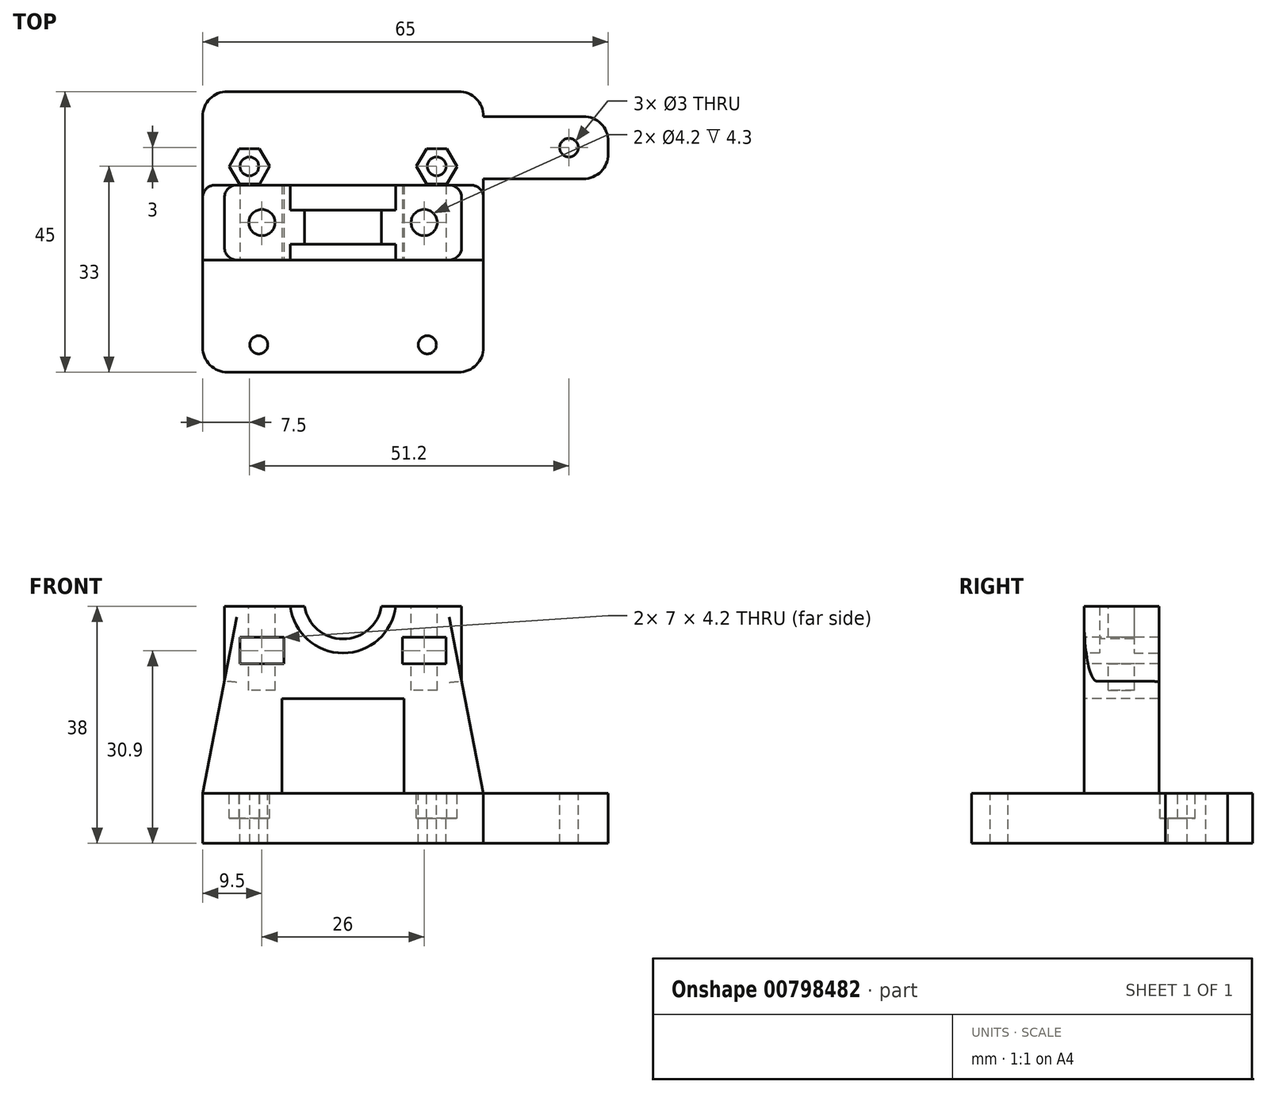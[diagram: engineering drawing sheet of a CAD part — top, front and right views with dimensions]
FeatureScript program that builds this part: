
annotation { "Feature Type Name" : "Feature", "Feature Type Description" : "" }
export const myFeature = defineFeature(function(context is Context, id is Id, definition is map)
    precondition{}
    {
        {
            var Q0;
            Q0=qCreatedBy(makeId("Top.planeOp"),FACE);
            var sketch = newSketch(context, id + "F0", { "sketchPlane" : qUnion([Q0])});
            skLineSegment(sketch, "E0.bottom", {"start": v(22.5, 22.5) * mm, "end": v(-22.5, 22.5) * mm});
            skLineSegment(sketch, "E0.top", {"start": v(22.5, -22.5) * mm, "end": v(-22.5, -22.5) * mm});
            skLineSegment(sketch, "E0.left", {"start": v(22.5, 22.5) * mm, "end": v(22.5, -22.5) * mm});
            skLineSegment(sketch, "E0.right", {"start": v(-22.5, 22.5) * mm, "end": v(-22.5, -22.5) * mm});
            skPoint(sketch, "E0.middle", {"position": v(0, 0) * mm});
            skLineSegment(sketch, "E1.bottom", {"start": v(22.5, 8.5) * mm, "end": v(42.5, 8.5) * mm});
            skLineSegment(sketch, "E1.top", {"start": v(22.5, 18.5) * mm, "end": v(42.5, 18.5) * mm});
            skLineSegment(sketch, "E1.left", {"start": v(22.5, 8.5) * mm, "end": v(22.5, 18.5) * mm});
            skLineSegment(sketch, "E1.right", {"start": v(42.5, 8.5) * mm, "end": v(42.5, 18.5) * mm});
            skSolve(sketch);
        }
        {
            var Q0;
            {var subQ3=sQuery(id+"F0.wireOp",EDGE,"E0.bottom");Q0=makeQuery(id+"F0.imprint","IMPRINT",FACE,{"disambiguationData":[TD([[makeQuery(id+"F0.imprint","IMPRINT",EDGE,{"derivedFrom":subQ3}),1.0]])]});}
            var Q1;
            Q1=makeQuery(id+"F0.imprint","IMPRINT",FACE,{"disambiguationData":[TD([[makeQuery(id+"F0.imprint","IMPRINT",EDGE,{"derivedFrom":sQuery(id+"F0.wireOp",EDGE,"E1.bottom")}),1.0]])]});
            extrude(context, id + "F1", {"entities" : qUnion([Q0, Q1]), "depth" : 8 * mm, "offsetDistance" : 25 * mm});
        }
        {
            var Q0;
            Q0=makeQuery(id+"F1.opExtrude","CAP_FACE",FACE,{"disambiguationData":[OSD([sQuery(id+"F0.wireOp",EDGE,"E0.bottom"),sQuery(id+"F0.wireOp",EDGE,"E0.top"),sQuery(id+"F0.wireOp",EDGE,"E0.left"),sQuery(id+"F0.wireOp",EDGE,"E0.right"),sQuery(id+"F0.wireOp",EDGE,"E1.bottom"),sQuery(id+"F0.wireOp",EDGE,"E1.top"),sQuery(id+"F0.wireOp",EDGE,"E1.right")])],"isStart":false});
            var sketch = newSketch(context, id + "F2", { "sketchPlane" : qUnion([Q0])});
            skLineSegment(sketch, "E2.bottom", {"start": v(-22.5, -4.5) * mm, "end": v(22.5, -4.5) * mm});
            skLineSegment(sketch, "E2.top", {"start": v(-22.5, 7.5) * mm, "end": v(22.5, 7.5) * mm});
            skLineSegment(sketch, "E2.left", {"start": v(-22.5, -4.5) * mm, "end": v(-22.5, 7.5) * mm});
            skLineSegment(sketch, "E2.right", {"start": v(22.5, -4.5) * mm, "end": v(22.5, 7.5) * mm});
            skSolve(sketch);
        }
        {
            var Q0;
            Q0=makeQuery(id+"F2.imprint","IMPRINT",FACE,{"disambiguationData":[TD([[makeQuery(id+"F2.imprint","IMPRINT",EDGE,{"derivedFrom":sQuery(id+"F2.wireOp",EDGE,"E2.bottom")}),1.0]])]});
            extrude(context, id + "F3", {"entities" : qUnion([Q0]), "operationType" : NewBodyOperationType.ADD, "depth" : 18 * mm, "offsetDistance" : 25 * mm});
        }
        {
            var Q0;
            Q0=makeQuery(id+"F3.opExtrude","CAP_FACE",FACE,{"disambiguationData":[OSD([sQuery(id+"F2.wireOp",EDGE,"E2.bottom"),sQuery(id+"F2.wireOp",EDGE,"E2.top"),sQuery(id+"F2.wireOp",EDGE,"E2.left"),sQuery(id+"F2.wireOp",EDGE,"E2.right")])],"isStart":false});
            var sketch = newSketch(context, id + "F4", { "sketchPlane" : qUnion([Q0])});
            skLineSegment(sketch, "E3.bottom", {"start": v(-19, 7.5) * mm, "end": v(19, 7.5) * mm});
            skLineSegment(sketch, "E3.top", {"start": v(-19, -4.5) * mm, "end": v(19, -4.5) * mm});
            skLineSegment(sketch, "E3.left", {"start": v(-19, 7.5) * mm, "end": v(-19, -4.5) * mm});
            skLineSegment(sketch, "E3.right", {"start": v(19, 7.5) * mm, "end": v(19, -4.5) * mm});
            skSolve(sketch);
        }
        {
            var Q0;
            Q0=makeQuery(id+"F4.imprint","IMPRINT",FACE,{"disambiguationData":[TD([[makeQuery(id+"F4.imprint","IMPRINT",EDGE,{"derivedFrom":sQuery(id+"F4.wireOp",EDGE,"E3.bottom")}),-1.0]])]});
            extrude(context, id + "F5", {"entities" : qUnion([Q0]), "operationType" : NewBodyOperationType.ADD, "depth" : 12 * mm, "offsetDistance" : 25 * mm});
        }
        {
            var Q0;
            Q0=makeQuery(id+"F5.boolean.opBoolean","MERGE",FACE,{"derivedFrom":[makeQuery(id+"F3.opExtrude","SWEPT_FACE",FACE,{"disambiguationData":[OSD([sQuery(id+"F2.wireOp",EDGE,"E2.bottom")])]}),makeQuery(id+"F5.opExtrude","SWEPT_FACE",FACE,{"disambiguationData":[OSD([sQuery(id+"F4.wireOp",EDGE,"E3.top")])]})]});
            var sketch = newSketch(context, id + "F6", { "sketchPlane" : qUnion([Q0])});
            skLineSegment(sketch, "E4", {"start": v(-19, 26) * mm, "end": v(-22.5, 8) * mm});
            skLineSegment(sketch, "E5", {"start": v(-22.5, 8) * mm, "end": v(-22.5, 26) * mm});
            skLineSegment(sketch, "E6", {"start": v(-22.5, 26) * mm, "end": v(-19, 26) * mm});
            skLineSegment(sketch, "E7", {"start": v(19, 26) * mm, "end": v(22.5, 26) * mm});
            skLineSegment(sketch, "E8", {"start": v(22.5, 26) * mm, "end": v(22.5, 8) * mm});
            skLineSegment(sketch, "E9", {"start": v(22.5, 8) * mm, "end": v(19, 26) * mm});
            skSolve(sketch);
        }
        {
            var Q0;
            Q0=makeQuery(id+"F6.imprint","IMPRINT",FACE,{"disambiguationData":[TD([[makeQuery(id+"F6.imprint","IMPRINT",EDGE,{"derivedFrom":sQuery(id+"F6.wireOp",EDGE,"E4")}),-1.0]])]});
            var Q1;
            Q1=makeQuery(id+"F6.imprint","IMPRINT",FACE,{"disambiguationData":[TD([[makeQuery(id+"F6.imprint","IMPRINT",EDGE,{"derivedFrom":sQuery(id+"F6.wireOp",EDGE,"E7")}),-1.0]])]});
            extrude(context, id + "F7", {"entities" : qUnion([Q0, Q1]), "operationType" : NewBodyOperationType.REMOVE, "oppositeDirection" : true, "depth" : 25 * mm, "offsetDistance" : 25 * mm});
        }
        {
            var Q0;
            Q0=makeQuery(id+"F5.boolean.opBoolean","MERGE",FACE,{"derivedFrom":[makeQuery(id+"F3.opExtrude","SWEPT_FACE",FACE,{"disambiguationData":[OSD([sQuery(id+"F2.wireOp",EDGE,"E2.bottom")])]}),makeQuery(id+"F5.opExtrude","SWEPT_FACE",FACE,{"disambiguationData":[OSD([sQuery(id+"F4.wireOp",EDGE,"E3.top")])]})]});
            var sketch = newSketch(context, id + "F8", { "sketchPlane" : qUnion([Q0])});
            skLineSegment(sketch, "E10.bottom", {"start": v(-9.8, 8) * mm, "end": v(9.8, 8) * mm});
            skLineSegment(sketch, "E10.top", {"start": v(-9.8, 23.2) * mm, "end": v(9.8, 23.2) * mm});
            skLineSegment(sketch, "E10.left", {"start": v(-9.8, 8) * mm, "end": v(-9.8, 23.2) * mm});
            skLineSegment(sketch, "E10.right", {"start": v(9.8, 8) * mm, "end": v(9.8, 23.2) * mm});
            skLineSegment(sketch, "E11", {"start": v(0, 0) * mm, "end": v(0, 8) * mm, "construction": true});
            skSolve(sketch);
        }
        {
            var Q0;
            Q0=makeQuery(id+"F8.imprint","IMPRINT",FACE,{"disambiguationData":[TD([[makeQuery(id+"F8.imprint","IMPRINT",EDGE,{"derivedFrom":sQuery(id+"F8.wireOp",EDGE,"E10.bottom")}),1.0]])]});
            extrude(context, id + "F9", {"entities" : qUnion([Q0]), "operationType" : NewBodyOperationType.REMOVE, "oppositeDirection" : true, "depth" : 25 * mm, "offsetDistance" : 25 * mm});
        }
        {
            var Q0;
            {var subQ0=sQuery(id+"F0.wireOp",EDGE,"E0.right");var subQ3=sQuery(id+"F0.wireOp",EDGE,"E0.left");var subQ4=sQuery(id+"F0.wireOp",EDGE,"E0.bottom");var subQ6=sQuery(id+"F0.wireOp",EDGE,"E1.top");var subQ7=sQuery(id+"F0.wireOp",EDGE,"E0.top");var subQ8=sQuery(id+"F0.wireOp",EDGE,"E1.bottom");var subQ11=sQuery(id+"F0.wireOp",EDGE,"E1.right");var subQ12=makeQuery(id+"F1.opExtrude","CAP_FACE",FACE,{"disambiguationData":[OSD([subQ4,subQ7,subQ3,subQ0,subQ8,subQ6,subQ11])],"isStart":false});Q0=makeQuery(id+"F9.boolean.opBoolean","MERGE",FACE,{"derivedFrom":[makeQuery(id+"F3.boolean.opBoolean","SPLIT",FACE,{"disambiguationData":[TD([makeQuery(id+"F1.opExtrude","SWEPT_FACE",FACE,{"disambiguationData":[OSD([subQ7])]})])],"derivedFrom":subQ12}),makeQuery(id+"F3.boolean.opBoolean","SPLIT",FACE,{"disambiguationData":[TD([makeQuery(id+"F1.opExtrude","SWEPT_FACE",FACE,{"disambiguationData":[OSD([subQ4])]})])],"derivedFrom":subQ12}),makeQuery(id+"F9.opExtrude","SWEPT_FACE",FACE,{"disambiguationData":[OSD([sQuery(id+"F8.wireOp",EDGE,"E10.bottom")])]})]});}
            var sketch = newSketch(context, id + "F10", { "sketchPlane" : qUnion([Q0])});
            skCircle(sketch, "E12", {"center": v(-15, 10.5) * mm, "radius": 1.5 * mm});
            skLineSegment(sketch, "E13", {"start": v(-15, 10.5) * mm, "end": v(15, 10.5) * mm, "construction": true});
            skCircle(sketch, "E14", {"center": v(15, 10.5) * mm, "radius": 1.5 * mm});
            skSolve(sketch);
        }
        {
            var Q0;
            Q0=makeQuery(id+"F10.imprint","IMPRINT",FACE,{"disambiguationData":[TD([[makeQuery(id+"F10.imprint","IMPRINT",EDGE,{"derivedFrom":sQuery(id+"F10.wireOp",EDGE,"E12")}),1.0]])]});
            var Q1;
            Q1=makeQuery(id+"F10.imprint","IMPRINT",FACE,{"disambiguationData":[TD([[makeQuery(id+"F10.imprint","IMPRINT",EDGE,{"derivedFrom":sQuery(id+"F10.wireOp",EDGE,"E14")}),1.0]])]});
            extrude(context, id + "F11", {"entities" : qUnion([Q0, Q1]), "operationType" : NewBodyOperationType.REMOVE, "oppositeDirection" : true, "depth" : 25 * mm, "offsetDistance" : 25 * mm});
        }
        {
            var Q0;
            {var subQ0=sQuery(id+"F0.wireOp",EDGE,"E0.right");var subQ3=sQuery(id+"F0.wireOp",EDGE,"E0.left");var subQ4=sQuery(id+"F0.wireOp",EDGE,"E0.bottom");var subQ6=sQuery(id+"F0.wireOp",EDGE,"E1.top");var subQ7=sQuery(id+"F0.wireOp",EDGE,"E0.top");var subQ8=sQuery(id+"F0.wireOp",EDGE,"E1.bottom");var subQ11=sQuery(id+"F0.wireOp",EDGE,"E1.right");var subQ12=makeQuery(id+"F1.opExtrude","CAP_FACE",FACE,{"disambiguationData":[OSD([subQ4,subQ7,subQ3,subQ0,subQ8,subQ6,subQ11])],"isStart":false});Q0=makeQuery(id+"F9.boolean.opBoolean","MERGE",FACE,{"derivedFrom":[makeQuery(id+"F3.boolean.opBoolean","SPLIT",FACE,{"disambiguationData":[TD([makeQuery(id+"F1.opExtrude","SWEPT_FACE",FACE,{"disambiguationData":[OSD([subQ7])]})])],"derivedFrom":subQ12}),makeQuery(id+"F3.boolean.opBoolean","SPLIT",FACE,{"disambiguationData":[TD([makeQuery(id+"F1.opExtrude","SWEPT_FACE",FACE,{"disambiguationData":[OSD([subQ4])]})])],"derivedFrom":subQ12}),makeQuery(id+"F9.opExtrude","SWEPT_FACE",FACE,{"disambiguationData":[OSD([sQuery(id+"F8.wireOp",EDGE,"E10.bottom")])]})]});}
            var sketch = newSketch(context, id + "F12", { "sketchPlane" : qUnion([Q0])});
            skCircle(sketch, "E15.cCircle", {"center": v(-15, 10.5) * mm, "radius": 3.25 * mm, "construction": true});
            skLineSegment(sketch, "E15.0", {"start": v(-13.4, 13.32) * mm, "end": v(-11.75, 10.52) * mm});
            skLineSegment(sketch, "E15.1", {"start": v(-11.75, 10.52) * mm, "end": v(-13.36, 7.7) * mm});
            skLineSegment(sketch, "E15.2", {"start": v(-13.36, 7.7) * mm, "end": v(-16.6, 7.68) * mm});
            skLineSegment(sketch, "E15.3", {"start": v(-16.6, 7.68) * mm, "end": v(-18.25, 10.48) * mm});
            skLineSegment(sketch, "E15.4", {"start": v(-18.25, 10.48) * mm, "end": v(-16.64, 13.3) * mm});
            skLineSegment(sketch, "E15.5", {"start": v(-16.64, 13.3) * mm, "end": v(-13.4, 13.32) * mm});
            skCircle(sketch, "E16.cCircle", {"center": v(15, 10.5) * mm, "radius": 3.25 * mm, "construction": true});
            skLineSegment(sketch, "E16.0", {"start": v(18.25, 10.48) * mm, "end": v(16.6, 7.68) * mm});
            skLineSegment(sketch, "E16.1", {"start": v(16.6, 7.68) * mm, "end": v(13.36, 7.7) * mm});
            skLineSegment(sketch, "E16.2", {"start": v(13.36, 7.7) * mm, "end": v(11.75, 10.52) * mm});
            skLineSegment(sketch, "E16.3", {"start": v(11.75, 10.52) * mm, "end": v(13.4, 13.32) * mm});
            skLineSegment(sketch, "E16.4", {"start": v(13.4, 13.32) * mm, "end": v(16.64, 13.3) * mm});
            skLineSegment(sketch, "E16.5", {"start": v(16.64, 13.3) * mm, "end": v(18.25, 10.48) * mm});
            skSolve(sketch);
        }
        {
            var Q0;
            Q0=makeQuery(id+"F12.imprint","IMPRINT",FACE,{"disambiguationData":[TD([[makeQuery(id+"F12.imprint","IMPRINT",EDGE,{"derivedFrom":sQuery(id+"F12.wireOp",EDGE,"E15.0")}),-1.0]])]});
            var Q1;
            Q1=makeQuery(id+"F12.imprint","IMPRINT",FACE,{"disambiguationData":[TD([[makeQuery(id+"F12.imprint","IMPRINT",EDGE,{"derivedFrom":sQuery(id+"F12.wireOp",EDGE,"E16.0")}),-1.0]])]});
            extrude(context, id + "F13", {"entities" : qUnion([Q0, Q1]), "operationType" : NewBodyOperationType.REMOVE, "oppositeDirection" : true, "depth" : 4 * mm, "offsetDistance" : 25 * mm});
        }
        {
            var Q0;
            Q0=makeQuery(id+"F5.boolean.opBoolean","MERGE",FACE,{"derivedFrom":[makeQuery(id+"F3.opExtrude","SWEPT_FACE",FACE,{"disambiguationData":[OSD([sQuery(id+"F2.wireOp",EDGE,"E2.bottom")])]}),makeQuery(id+"F5.opExtrude","SWEPT_FACE",FACE,{"disambiguationData":[OSD([sQuery(id+"F4.wireOp",EDGE,"E3.top")])]})]});
            var sketch = newSketch(context, id + "F14", { "sketchPlane" : qUnion([Q0])});
            skLineSegment(sketch, "E17", {"start": v(0, 38) * mm, "end": v(0, 39) * mm, "construction": true});
            skCircle(sketch, "E18", {"center": v(0, 39) * mm, "radius": 8.5 * mm});
            skCircle(sketch, "E19", {"center": v(0, 39) * mm, "radius": 6.25 * mm});
            skSolve(sketch);
        }
        {
            var Q0;
            Q0=qSketchRegion(id+"F14",true);
            extrude(context, id + "F15", {"entities" : qUnion([Q0]), "operationType" : NewBodyOperationType.REMOVE, "oppositeDirection" : true, "depth" : 2.5 * mm, "offsetDistance" : 25 * mm});
        }
        {
            var Q0;
            {var subQ0=sQuery(id+"F0.wireOp",EDGE,"E0.right");var subQ3=sQuery(id+"F0.wireOp",EDGE,"E0.left");var subQ4=sQuery(id+"F0.wireOp",EDGE,"E0.bottom");var subQ6=sQuery(id+"F0.wireOp",EDGE,"E1.top");var subQ7=sQuery(id+"F0.wireOp",EDGE,"E0.top");var subQ8=sQuery(id+"F0.wireOp",EDGE,"E1.bottom");var subQ11=sQuery(id+"F0.wireOp",EDGE,"E1.right");var subQ12=makeQuery(id+"F1.opExtrude","CAP_FACE",FACE,{"disambiguationData":[OSD([subQ4,subQ7,subQ3,subQ0,subQ8,subQ6,subQ11])],"isStart":false});Q0=makeQuery(id+"F9.boolean.opBoolean","MERGE",FACE,{"derivedFrom":[makeQuery(id+"F3.boolean.opBoolean","SPLIT",FACE,{"disambiguationData":[TD([makeQuery(id+"F1.opExtrude","SWEPT_FACE",FACE,{"disambiguationData":[OSD([subQ7])]})])],"derivedFrom":subQ12}),makeQuery(id+"F3.boolean.opBoolean","SPLIT",FACE,{"disambiguationData":[TD([makeQuery(id+"F1.opExtrude","SWEPT_FACE",FACE,{"disambiguationData":[OSD([subQ4])]})])],"derivedFrom":subQ12}),makeQuery(id+"F9.opExtrude","SWEPT_FACE",FACE,{"disambiguationData":[OSD([sQuery(id+"F8.wireOp",EDGE,"E10.bottom")])]})]});}
            var sketch = newSketch(context, id + "F16", { "sketchPlane" : qUnion([Q0])});
            skCircle(sketch, "E20", {"center": v(36.2, 13.5) * mm, "radius": 1.5 * mm});
            skPoint(sketch, "E20.centerSnap0", {"position": v(42.5, 13.5) * mm});
            skSolve(sketch);
        }
        {
            var Q0;
            Q0=makeQuery(id+"F16.imprint","IMPRINT",FACE,{"disambiguationData":[TD([[makeQuery(id+"F16.imprint","IMPRINT",EDGE,{"derivedFrom":sQuery(id+"F16.wireOp",EDGE,"E20")}),1.0]])]});
            extrude(context, id + "F17", {"entities" : qUnion([Q0]), "operationType" : NewBodyOperationType.REMOVE, "oppositeDirection" : true, "depth" : 25 * mm, "offsetDistance" : 25 * mm});
        }
        {
            var Q0;
            {var subQ0=sQuery(id+"F4.wireOp",EDGE,"E3.top");var subQ1=sQuery(id+"F4.wireOp",EDGE,"E3.bottom");var subQ2=sQuery(id+"F4.wireOp",EDGE,"E3.left");Q0=makeQuery(id+"FmUpQ3kPXyIInFc_1.boolean.opBoolean","SPLIT",FACE,{"disambiguationData":[TD([makeQuery(id+"F5.opExtrude","SWEPT_FACE",FACE,{"disambiguationData":[OSD([subQ2])]})])],"derivedFrom":makeQuery(id+"F5.opExtrude","CAP_FACE",FACE,{"disambiguationData":[OSD([subQ1,subQ0,subQ2,sQuery(id+"F4.wireOp",EDGE,"E3.right")])],"isStart":false})});}
            var sketch = newSketch(context, id + "F18", { "sketchPlane" : qUnion([Q0])});
            skPoint(sketch, "E21.centerSnap0", {"position": v(0, 7.5) * mm});
            skPoint(sketch, "E21.centerSnap1", {"position": v(-19, 1.5) * mm});
            skCircle(sketch, "E22", {"center": v(13, 1.5) * mm, "radius": 2.1 * mm});
            skCircle(sketch, "E23", {"center": v(-13, 1.5) * mm, "radius": 2.1 * mm});
            skSolve(sketch);
        }
        {
            var Q0;
            Q0=makeQuery(id+"F18.imprint","IMPRINT",FACE,{"disambiguationData":[TD([[makeQuery(id+"F18.imprint","IMPRINT",EDGE,{"derivedFrom":sQuery(id+"F18.wireOp",EDGE,"E21")}),1.0]])]});
            var Q1;
            Q1=makeQuery(id+"F18.imprint","IMPRINT",FACE,{"disambiguationData":[TD([[makeQuery(id+"F18.imprint","IMPRINT",EDGE,{"derivedFrom":sQuery(id+"F18.wireOp",EDGE,"E22")}),1.0]])]});
            var Q2;
            Q2=makeQuery(id+"F18.imprint","IMPRINT",FACE,{"disambiguationData":[TD([[makeQuery(id+"F18.imprint","IMPRINT",EDGE,{"derivedFrom":sQuery(id+"F18.wireOp",EDGE,"E23")}),1.0]])]});
            extrude(context, id + "F19", {"entities" : qUnion([Q0, Q1, Q2]), "operationType" : NewBodyOperationType.REMOVE, "oppositeDirection" : true, "depth" : 13.5 * mm, "offsetDistance" : 25 * mm});
        }
        {
            var Q0;
            Q0=makeQuery(id+"F5.boolean.opBoolean","MERGE",FACE,{"derivedFrom":[makeQuery(id+"F3.opExtrude","SWEPT_FACE",FACE,{"disambiguationData":[OSD([sQuery(id+"F2.wireOp",EDGE,"E2.bottom")])]}),makeQuery(id+"F5.opExtrude","SWEPT_FACE",FACE,{"disambiguationData":[OSD([sQuery(id+"F4.wireOp",EDGE,"E3.top")])]})]});
            var sketch = newSketch(context, id + "F20", { "sketchPlane" : qUnion([Q0])});
            skLineSegment(sketch, "E24.bottom", {"start": v(-16.5, 33) * mm, "end": v(-9.5, 33) * mm});
            skLineSegment(sketch, "E24.top", {"start": v(-16.5, 28.8) * mm, "end": v(-9.5, 28.8) * mm});
            skLineSegment(sketch, "E24.left", {"start": v(-16.5, 33) * mm, "end": v(-16.5, 28.8) * mm});
            skLineSegment(sketch, "E24.right", {"start": v(-9.5, 33) * mm, "end": v(-9.5, 28.8) * mm});
            skLineSegment(sketch, "E25.bottom", {"start": v(16.5, 33) * mm, "end": v(9.5, 33) * mm});
            skLineSegment(sketch, "E25.top", {"start": v(16.5, 28.8) * mm, "end": v(9.5, 28.8) * mm});
            skLineSegment(sketch, "E25.left", {"start": v(16.5, 33) * mm, "end": v(16.5, 28.8) * mm});
            skLineSegment(sketch, "E25.right", {"start": v(9.5, 33) * mm, "end": v(9.5, 28.8) * mm});
            skSolve(sketch);
        }
        {
            var Q0;
            Q0=makeQuery(id+"F20.imprint","IMPRINT",FACE,{"disambiguationData":[TD([[makeQuery(id+"F20.imprint","IMPRINT",EDGE,{"derivedFrom":sQuery(id+"F20.wireOp",EDGE,"E24.bottom")}),-1.0]])]});
            var Q1;
            Q1=makeQuery(id+"F20.imprint","IMPRINT",FACE,{"disambiguationData":[TD([[makeQuery(id+"F20.imprint","IMPRINT",EDGE,{"derivedFrom":sQuery(id+"F20.wireOp",EDGE,"E25.bottom")}),1.0]])]});
            extrude(context, id + "F21", {"entities" : qUnion([Q0, Q1]), "operationType" : NewBodyOperationType.REMOVE, "oppositeDirection" : true, "depth" : 25 * mm, "offsetDistance" : 25 * mm});
        }
        {
            var Q0;
            {var subQ0=sQuery(id+"F0.wireOp",EDGE,"E0.right");var subQ3=sQuery(id+"F0.wireOp",EDGE,"E0.left");var subQ4=sQuery(id+"F0.wireOp",EDGE,"E0.bottom");var subQ6=sQuery(id+"F0.wireOp",EDGE,"E1.top");var subQ7=sQuery(id+"F0.wireOp",EDGE,"E0.top");var subQ8=sQuery(id+"F0.wireOp",EDGE,"E1.bottom");var subQ11=sQuery(id+"F0.wireOp",EDGE,"E1.right");var subQ12=makeQuery(id+"F1.opExtrude","CAP_FACE",FACE,{"disambiguationData":[OSD([subQ4,subQ7,subQ3,subQ0,subQ8,subQ6,subQ11])],"isStart":false});Q0=makeQuery(id+"F9.boolean.opBoolean","MERGE",FACE,{"derivedFrom":[makeQuery(id+"F3.boolean.opBoolean","SPLIT",FACE,{"disambiguationData":[TD([makeQuery(id+"F1.opExtrude","SWEPT_FACE",FACE,{"disambiguationData":[OSD([subQ7])]})])],"derivedFrom":subQ12}),makeQuery(id+"F3.boolean.opBoolean","SPLIT",FACE,{"disambiguationData":[TD([makeQuery(id+"F1.opExtrude","SWEPT_FACE",FACE,{"disambiguationData":[OSD([subQ4])]})])],"derivedFrom":subQ12}),makeQuery(id+"F9.opExtrude","SWEPT_FACE",FACE,{"disambiguationData":[OSD([sQuery(id+"F8.wireOp",EDGE,"E10.bottom")])]})]});}
            var sketch = newSketch(context, id + "F22", { "sketchPlane" : qUnion([Q0])});
            skCircle(sketch, "E26", {"center": v(-13.5, -18.1) * mm, "radius": 1.45 * mm});
            skCircle(sketch, "E27", {"center": v(13.5, -18.1) * mm, "radius": 1.45 * mm});
            skSolve(sketch);
        }
        {
            var Q0;
            Q0=makeQuery(id+"F22.imprint","IMPRINT",FACE,{"disambiguationData":[TD([[makeQuery(id+"F22.imprint","IMPRINT",EDGE,{"derivedFrom":sQuery(id+"F22.wireOp",EDGE,"E26")}),1.0]])]});
            var Q1;
            Q1=makeQuery(id+"F22.imprint","IMPRINT",FACE,{"disambiguationData":[TD([[makeQuery(id+"F22.imprint","IMPRINT",EDGE,{"derivedFrom":sQuery(id+"F22.wireOp",EDGE,"E27")}),1.0]])]});
            extrude(context, id + "F23", {"entities" : qUnion([Q0, Q1]), "operationType" : NewBodyOperationType.REMOVE, "oppositeDirection" : true, "depth" : 25 * mm, "offsetDistance" : 25 * mm});
        }
        {
            var Q0;
            Q0=makeQuery(id+"F1.opExtrude","SWEPT_EDGE",EDGE,{"disambiguationData":[OSD([sQuery(id+"F0.wireOp",EDGE,"E0.top"),sQuery(id+"F0.wireOp",EDGE,"E0.right")])]});
            var Q1;
            Q1=makeQuery(id+"F1.opExtrude","SWEPT_EDGE",EDGE,{"disambiguationData":[OSD([sQuery(id+"F0.wireOp",EDGE,"E0.top"),sQuery(id+"F0.wireOp",EDGE,"E0.left")])]});
            var Q2;
            Q2=makeQuery(id+"F1.opExtrude","SWEPT_EDGE",EDGE,{"disambiguationData":[OSD([sQuery(id+"F0.wireOp",EDGE,"E1.bottom"),sQuery(id+"F0.wireOp",EDGE,"E1.right")])]});
            var Q3;
            Q3=makeQuery(id+"F1.opExtrude","SWEPT_EDGE",EDGE,{"disambiguationData":[OSD([sQuery(id+"F0.wireOp",EDGE,"E1.top"),sQuery(id+"F0.wireOp",EDGE,"E1.right")])]});
            var Q4;
            Q4=makeQuery(id+"F1.opExtrude","SWEPT_EDGE",EDGE,{"disambiguationData":[OSD([sQuery(id+"F0.wireOp",EDGE,"E0.bottom"),sQuery(id+"F0.wireOp",EDGE,"E0.left")])]});
            var Q5;
            Q5=makeQuery(id+"F1.opExtrude","SWEPT_EDGE",EDGE,{"disambiguationData":[OSD([sQuery(id+"F0.wireOp",EDGE,"E0.bottom"),sQuery(id+"F0.wireOp",EDGE,"E0.right")])]});
            fillet(context, id + "F24", {"entities" : qUnion([Q0, Q1, Q2, Q3, Q4, Q5]), "radius" : 4 * mm, "tangentPropagation" : true, "allowEdgeOverflow" : false});
        }
        {
            var Q0;
            Q0=makeQuery(id+"F7.boolean.opBoolean","COPY",EDGE,{"derivedFrom":makeQuery(id+"F7.opExtrude","CAP_EDGE",EDGE,{"disambiguationData":[OSD([sQuery(id+"F6.wireOp",EDGE,"E4")])],"isStart":true})});
            var Q1;
            Q1=makeQuery(id+"F7.boolean.opBoolean","COPY",EDGE,{"derivedFrom":makeQuery(id+"F7.opExtrude","CAP_EDGE",EDGE,{"disambiguationData":[OSD([sQuery(id+"F6.wireOp",EDGE,"E9")])],"isStart":true})});
            var Q2;
            Q2=makeQuery(id+"F7.boolean.opBoolean","INTERSECT",EDGE,{"derivedFrom":[makeQuery(id+"F5.boolean.opBoolean","MERGE",FACE,{"derivedFrom":[makeQuery(id+"F3.opExtrude","SWEPT_FACE",FACE,{"disambiguationData":[OSD([sQuery(id+"F2.wireOp",EDGE,"E2.top")])]}),makeQuery(id+"F5.opExtrude","SWEPT_FACE",FACE,{"disambiguationData":[OSD([sQuery(id+"F4.wireOp",EDGE,"E3.bottom")])]})]}),makeQuery(id+"F7.opExtrude","SWEPT_FACE",FACE,{"disambiguationData":[OSD([sQuery(id+"F6.wireOp",EDGE,"E9")])]})]});
            var Q3;
            Q3=makeQuery(id+"F7.boolean.opBoolean","INTERSECT",EDGE,{"derivedFrom":[makeQuery(id+"F5.boolean.opBoolean","MERGE",FACE,{"derivedFrom":[makeQuery(id+"F3.opExtrude","SWEPT_FACE",FACE,{"disambiguationData":[OSD([sQuery(id+"F2.wireOp",EDGE,"E2.top")])]}),makeQuery(id+"F5.opExtrude","SWEPT_FACE",FACE,{"disambiguationData":[OSD([sQuery(id+"F4.wireOp",EDGE,"E3.bottom")])]})]}),makeQuery(id+"F7.opExtrude","SWEPT_FACE",FACE,{"disambiguationData":[OSD([sQuery(id+"F6.wireOp",EDGE,"E4")])]})]});
            var Q4;
            Q4=makeQuery(id+"F5.opExtrude","SWEPT_EDGE",EDGE,{"disambiguationData":[OSD([sQuery(id+"F2.wireOp",EDGE,"E2.bottom"),sQuery(id+"F4.wireOp",EDGE,"E3.top"),sQuery(id+"F4.wireOp",EDGE,"E3.right")])]});
            var Q5;
            Q5=makeQuery(id+"F5.opExtrude","SWEPT_EDGE",EDGE,{"disambiguationData":[OSD([sQuery(id+"F2.wireOp",EDGE,"E2.top"),sQuery(id+"F4.wireOp",EDGE,"E3.bottom"),sQuery(id+"F4.wireOp",EDGE,"E3.right")])]});
            var Q6;
            Q6=makeQuery(id+"F5.opExtrude","SWEPT_EDGE",EDGE,{"disambiguationData":[OSD([sQuery(id+"F2.wireOp",EDGE,"E2.top"),sQuery(id+"F4.wireOp",EDGE,"E3.bottom"),sQuery(id+"F4.wireOp",EDGE,"E3.left")])]});
            var Q7;
            Q7=makeQuery(id+"F5.opExtrude","SWEPT_EDGE",EDGE,{"disambiguationData":[OSD([sQuery(id+"F2.wireOp",EDGE,"E2.bottom"),sQuery(id+"F4.wireOp",EDGE,"E3.top"),sQuery(id+"F4.wireOp",EDGE,"E3.left")])]});
            fillet(context, id + "F25", {"entities" : qUnion([Q0, Q1, Q2, Q3, Q4, Q5, Q6, Q7]), "radius" : 2 * mm, "tangentPropagation" : true, "allowEdgeOverflow" : false});
        }
        {
            var Q0;
            {var subQ0=sQuery(id+"F4.wireOp",EDGE,"E3.top");Q0=makeQuery(id+"F15.boolean.opBoolean","SPLIT",FACE,{"disambiguationData":[TD([makeQuery(id+"F15.opExtrude","SWEPT_FACE",FACE,{"disambiguationData":[OSD([sQuery(id+"F14.wireOp",EDGE,"E19")])]})])],"derivedFrom":makeQuery(id+"F5.boolean.opBoolean","MERGE",FACE,{"derivedFrom":[makeQuery(id+"F3.opExtrude","SWEPT_FACE",FACE,{"disambiguationData":[OSD([sQuery(id+"F2.wireOp",EDGE,"E2.bottom")])]}),makeQuery(id+"F5.opExtrude","SWEPT_FACE",FACE,{"disambiguationData":[OSD([subQ0])]})]})});}
            extrude(context, id + "F26", {"entities" : qUnion([Q0]), "operationType" : NewBodyOperationType.REMOVE, "oppositeDirection" : true, "depth" : 25 * mm, "offsetDistance" : 25 * mm});
        }
        {
            var Q0;
            Q0=makeQuery(id+"F5.boolean.opBoolean","MERGE",FACE,{"derivedFrom":[makeQuery(id+"F3.opExtrude","SWEPT_FACE",FACE,{"disambiguationData":[OSD([sQuery(id+"F2.wireOp",EDGE,"E2.top")])]}),makeQuery(id+"F5.opExtrude","SWEPT_FACE",FACE,{"disambiguationData":[OSD([sQuery(id+"F4.wireOp",EDGE,"E3.bottom")])]})]});
            var sketch = newSketch(context, id + "F27", { "sketchPlane" : qUnion([Q0])});
            skLineSegment(sketch, "E28", {"start": v(-6.17, 38) * mm, "end": v(6.17, 38) * mm, "construction": true});
            skLineSegment(sketch, "E29", {"start": v(0, 38) * mm, "end": v(0, 39) * mm, "construction": true});
            skCircle(sketch, "E30", {"center": v(0, 39) * mm, "radius": 8.5 * mm});
            skSolve(sketch);
        }
        {
            var Q0;
            {var subQ3=sQuery(id+"F4.wireOp",EDGE,"E3.bottom");var subQ5=sQuery(id+"F2.wireOp",EDGE,"E2.top");var subQ6=makeQuery(id+"F5.opExtrude","SWEPT_FACE",FACE,{"disambiguationData":[OSD([subQ3])]});var subQ7=makeQuery(id+"F3.opExtrude","SWEPT_FACE",FACE,{"disambiguationData":[OSD([subQ5])]});var subQ8=makeQuery(id+"F26.opExtrude","SWEPT_FACE",FACE,{"disambiguationData":[OSD([sQuery(id+"F14.wireOp",EDGE,"E19")])]});var subQ14=makeQuery(id+"F26.boolean.opBoolean","INTERSECT",EDGE,{"derivedFrom":[makeQuery(id+"F5.boolean.opBoolean","MERGE",FACE,{"derivedFrom":[subQ7,subQ6]}),subQ8]});Q0=makeQuery(id+"F27.imprint","IMPRINT",FACE,{"disambiguationData":[TD([[makeQuery(id+"F27.imprint","IMPRINT",EDGE,{"derivedFrom":subQ14}),-1.0]])]});}
            extrude(context, id + "F28", {"entities" : qUnion([Q0]), "operationType" : NewBodyOperationType.REMOVE, "oppositeDirection" : true, "depth" : 4 * mm, "offsetDistance" : 25 * mm});
        }
    });
